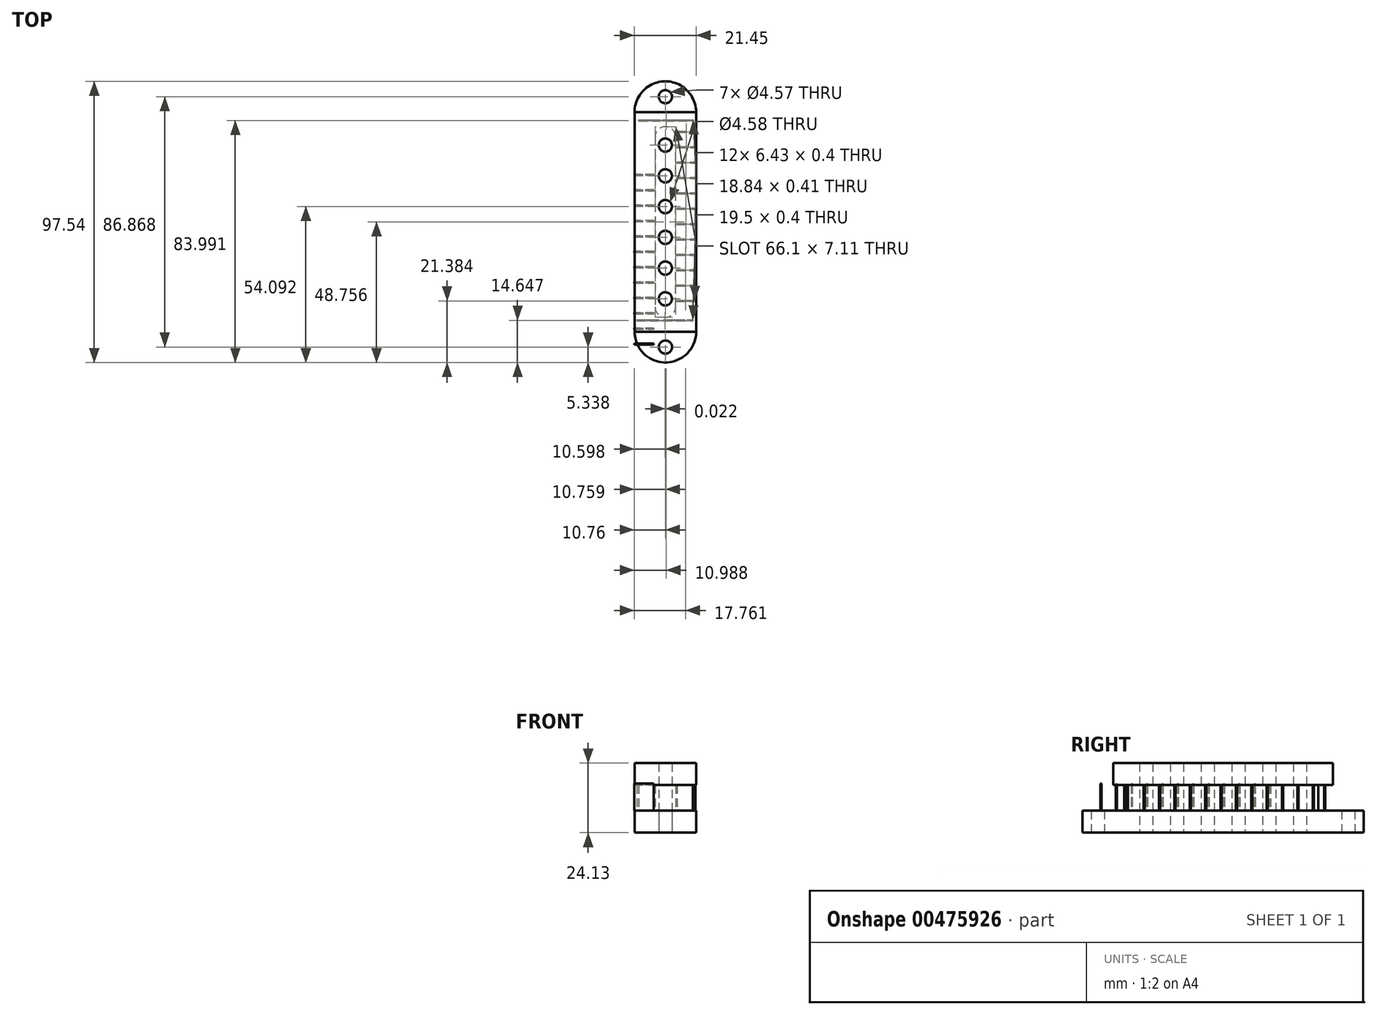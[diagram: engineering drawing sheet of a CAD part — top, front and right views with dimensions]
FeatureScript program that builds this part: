
annotation { "Feature Type Name" : "Feature", "Feature Type Description" : "" }
export const myFeature = defineFeature(function(context is Context, id is Id, definition is map)
    precondition{}
    {
        {
            var Q0;
            Q0=qCreatedBy(makeId("Top.planeOp"),FACE);
            var sketch = newSketch(context, id + "F0", { "sketchPlane" : qUnion([Q0])});
            skPoint(sketch, "E0.end.orphan", {"position": v(0, 0) * mm});
            skCircle(sketch, "E1", {"center": v(0, 12.62) * mm, "radius": 2.29 * mm});
            skCircle(sketch, "E2", {"center": v(0, 1.95) * mm, "radius": 2.29 * mm});
            skCircle(sketch, "E3", {"center": v(0, -8.72) * mm, "radius": 2.29 * mm});
            skCircle(sketch, "E4", {"center": v(0, -19.39) * mm, "radius": 2.29 * mm});
            skCircle(sketch, "E5", {"center": v(0, -30.06) * mm, "radius": 2.29 * mm});
            skCircle(sketch, "E6", {"center": v(0, -40.73) * mm, "radius": 2.29 * mm});
            skLineSegment(sketch, "E7", {"start": v(0, 24.06) * mm, "end": v(0, 14.92) * mm});
            skLineSegment(sketch, "E8", {"start": v(0, -52.14) * mm, "end": v(0, -43) * mm});
            skLineSegment(sketch, "E9", {"start": v(10.66, 24.07) * mm, "end": v(10.69, -52.13) * mm});
            skLineSegment(sketch, "E10", {"start": v(-10.69, 24.06) * mm, "end": v(-10.65, -52.14) * mm});
            skLineSegment(sketch, "E11", {"start": v(-10.69, 24.06) * mm, "end": v(10.66, 24.07) * mm});
            skLineSegment(sketch, "E12", {"start": v(-10.65, -52.14) * mm, "end": v(10.69, -52.13) * mm});
            skArc(sketch, "E13", {"start": v(-10.65, -52.14) * mm, "mid": v(0.03, -62.8) * mm, "end": v(10.69, -52.13) * mm});
            skArc(sketch, "E14", {"start": v(10.66, 24.07) * mm, "mid": v(-0.02, 34.73) * mm, "end": v(-10.69, 24.06) * mm});
            skCircle(sketch, "E15", {"center": v(0, 29.4) * mm, "radius": 2.29 * mm});
            skCircle(sketch, "E16", {"center": v(0.02, -57.47) * mm, "radius": 2.29 * mm});
            skSolve(sketch);
        }
        {
            var Q0;
            Q0 = qSketchRegion(id + "F0", true);
            extrude(context, id + "F1", {"entities" : qUnion([Q0]), "depth" : 7.62 * mm, "offsetDistance" : 25.4 * mm});
        }
        {
            var Q0;
            Q0=qCreatedBy(makeId("Top.planeOp"),FACE);
            var sketch = newSketch(context, id + "F2", { "sketchPlane" : qUnion([Q0])});
            skLineSegment(sketch, "E17", {"start": v(0, 0) * mm, "end": v(3.56, 0) * mm});
            skLineSegment(sketch, "E18", {"start": v(3.56, 0) * mm, "end": v(3.56, -43.55) * mm});
            skLineSegment(sketch, "E19", {"start": v(3.56, -43.55) * mm, "end": v(0, -43.55) * mm});
            skLineSegment(sketch, "E20", {"start": v(0, -43.55) * mm, "end": v(-3.56, -43.55) * mm});
            skPoint(sketch, "E20.endSnap0", {"position": v(1.78, -43.55) * mm});
            skLineSegment(sketch, "E21", {"start": v(-3.56, -43.55) * mm, "end": v(-3.56, 15.44) * mm});
            skLineSegment(sketch, "E22", {"start": v(-3.56, 15.44) * mm, "end": v(0, 15.44) * mm});
            skLineSegment(sketch, "E23", {"start": v(0, 15.44) * mm, "end": v(3.56, 15.44) * mm});
            skLineSegment(sketch, "E24", {"start": v(3.56, 15.44) * mm, "end": v(3.56, 0) * mm});
            skArc(sketch, "E25", {"start": v(-3.56, -43.55) * mm, "mid": v(0, -47.1) * mm, "end": v(3.56, -43.55) * mm});
            skArc(sketch, "E26", {"start": v(3.56, 15.44) * mm, "mid": v(0, 19) * mm, "end": v(-3.56, 15.44) * mm});
            skSolve(sketch);
        }
        {
            var Q0;
            Q0 = qSketchRegion(id + "F2", true);
            extrude(context, id + "F3", {"entities" : qUnion([Q0]), "operationType" : NewBodyOperationType.ADD, "depth" : 16.5 * mm, "offsetDistance" : 25.4 * mm});
        }
        {
            var Q0;
            Q0=makeQuery(id+"F3.opExtrude","CAP_FACE",FACE,{"disambiguationData":[OSD([sQuery(id+"F2.wireOp",EDGE,"E18"),sQuery(id+"F2.wireOp",EDGE,"E21"),sQuery(id+"F2.wireOp",EDGE,"E24"),sQuery(id+"F2.wireOp",EDGE,"E25"),sQuery(id+"F2.wireOp",EDGE,"E26")])],"isStart":false});
            var sketch = newSketch(context, id + "F4", { "sketchPlane" : qUnion([Q0])});
            skLineSegment(sketch, "E27", {"start": v(10.67, 0) * mm, "end": v(10.67, -52.15) * mm});
            skLineSegment(sketch, "E28", {"start": v(10.67, -52.15) * mm, "end": v(-10.67, -52.15) * mm});
            skLineSegment(sketch, "E29", {"start": v(-10.67, -52.15) * mm, "end": v(-10.67, 0) * mm});
            skLineSegment(sketch, "E30", {"start": v(-10.67, 0) * mm, "end": v(-10.67, 24.05) * mm});
            skLineSegment(sketch, "E31", {"start": v(-10.67, 24.05) * mm, "end": v(10.67, 24.05) * mm});
            skLineSegment(sketch, "E32", {"start": v(10.67, 24.05) * mm, "end": v(10.67, 0) * mm});
            skSolve(sketch);
        }
        {
            var Q0;
            Q0 = qSketchRegion(id + "F4", true);
            extrude(context, id + "F5", {"entities" : qUnion([Q0]), "operationType" : NewBodyOperationType.ADD, "depth" : 7.62 * mm, "offsetDistance" : 25.4 * mm});
        }
        {
            var Q0;
            Q0=makeQuery(id+"F0.imprint","IMPRINT",FACE,{"disambiguationData":[TD([[makeQuery(id+"F0.imprint","IMPRINT",EDGE,{"derivedFrom":sQuery(id+"F0.wireOp",EDGE,"E4")}),1.0]])]});
            var Q1;
            Q1=makeQuery(id+"F0.imprint","IMPRINT",FACE,{"disambiguationData":[TD([[makeQuery(id+"F0.imprint","IMPRINT",EDGE,{"derivedFrom":sQuery(id+"F0.wireOp",EDGE,"E6")}),1.0]])]});
            var Q2;
            Q2=makeQuery(id+"F0.imprint","IMPRINT",FACE,{"disambiguationData":[TD([[makeQuery(id+"F0.imprint","IMPRINT",EDGE,{"derivedFrom":sQuery(id+"F0.wireOp",EDGE,"E5")}),1.0]])]});
            var Q3;
            Q3=makeQuery(id+"F0.imprint","IMPRINT",FACE,{"disambiguationData":[TD([[makeQuery(id+"F0.imprint","IMPRINT",EDGE,{"derivedFrom":sQuery(id+"F0.wireOp",EDGE,"E3")}),1.0]])]});
            var Q4;
            Q4=makeQuery(id+"F0.imprint","IMPRINT",FACE,{"disambiguationData":[TD([[makeQuery(id+"F0.imprint","IMPRINT",EDGE,{"derivedFrom":sQuery(id+"F0.wireOp",EDGE,"E2")}),1.0]])]});
            var Q5;
            Q5=makeQuery(id+"F0.imprint","IMPRINT",FACE,{"disambiguationData":[TD([[makeQuery(id+"F0.imprint","IMPRINT",EDGE,{"derivedFrom":sQuery(id+"F0.wireOp",EDGE,"E1")}),1.0]])]});
            extrude(context, id + "F6", {"entities" : qUnion([Q0, Q1, Q2, Q3, Q4, Q5]), "operationType" : NewBodyOperationType.REMOVE, "endBound" : BoundingType.THROUGH_ALL, "depth" : 25.4 * mm, "offsetDistance" : 25.4 * mm});
        }
        {
            var Q0;
            Q0=makeQuery(id+"F1.opExtrude","CAP_FACE",FACE,{"disambiguationData":[OSD([sQuery(id+"F0.wireOp",EDGE,"E1"),sQuery(id+"F0.wireOp",EDGE,"E2"),sQuery(id+"F0.wireOp",EDGE,"E3"),sQuery(id+"F0.wireOp",EDGE,"E4"),sQuery(id+"F0.wireOp",EDGE,"E5"),sQuery(id+"F0.wireOp",EDGE,"E6"),sQuery(id+"F0.wireOp",EDGE,"E9"),sQuery(id+"F0.wireOp",EDGE,"E10"),sQuery(id+"F0.wireOp",EDGE,"E13"),sQuery(id+"F0.wireOp",EDGE,"E14"),sQuery(id+"F0.wireOp",EDGE,"E15"),sQuery(id+"F0.wireOp",EDGE,"E16")])],"isStart":false});
            var sketch = newSketch(context, id + "F7", { "sketchPlane" : qUnion([Q0])});
            skLineSegment(sketch, "E33.bottom", {"start": v(3.79, -41.63) * mm, "end": v(10.21, -41.63) * mm});
            skLineSegment(sketch, "E33.top", {"start": v(3.79, -41.23) * mm, "end": v(10.21, -41.23) * mm});
            skLineSegment(sketch, "E33.left", {"start": v(3.79, -41.63) * mm, "end": v(3.79, -41.23) * mm});
            skLineSegment(sketch, "E33.right", {"start": v(10.21, -41.63) * mm, "end": v(10.21, -41.23) * mm});
            skLineSegment(sketch, "E34.bottom", {"start": v(-9.91, -47.96) * mm, "end": v(9.59, -47.96) * mm});
            skLineSegment(sketch, "E34.top", {"start": v(-9.91, -48.36) * mm, "end": v(9.59, -48.36) * mm});
            skLineSegment(sketch, "E34.left", {"start": v(-9.91, -47.96) * mm, "end": v(-9.91, -48.36) * mm});
            skLineSegment(sketch, "E34.right", {"start": v(9.59, -47.96) * mm, "end": v(9.59, -48.36) * mm});
            skLineSegment(sketch, "E35.0.1.0", {"start": v(3.8, -36.3) * mm, "end": v(3.8, -35.9) * mm});
            skLineSegment(sketch, "E35.0.1.1", {"start": v(3.8, -35.9) * mm, "end": v(10.24, -35.9) * mm});
            skLineSegment(sketch, "E35.0.1.2", {"start": v(10.24, -36.3) * mm, "end": v(10.24, -35.9) * mm});
            skLineSegment(sketch, "E35.0.1.3", {"start": v(3.8, -36.3) * mm, "end": v(10.24, -36.3) * mm});
            skLineSegment(sketch, "E35.0.2.0", {"start": v(3.83, -30.96) * mm, "end": v(3.83, -30.56) * mm});
            skLineSegment(sketch, "E35.0.2.1", {"start": v(3.83, -30.56) * mm, "end": v(10.26, -30.56) * mm});
            skLineSegment(sketch, "E35.0.2.2", {"start": v(10.26, -30.96) * mm, "end": v(10.26, -30.56) * mm});
            skLineSegment(sketch, "E35.0.2.3", {"start": v(3.83, -30.96) * mm, "end": v(10.26, -30.96) * mm});
            skLineSegment(sketch, "E35.0.3.0", {"start": v(3.85, -25.62) * mm, "end": v(3.85, -25.22) * mm});
            skLineSegment(sketch, "E35.0.3.1", {"start": v(3.85, -25.22) * mm, "end": v(10.28, -25.22) * mm});
            skLineSegment(sketch, "E35.0.3.2", {"start": v(10.28, -25.62) * mm, "end": v(10.28, -25.22) * mm});
            skLineSegment(sketch, "E35.0.3.3", {"start": v(3.85, -25.62) * mm, "end": v(10.28, -25.62) * mm});
            skLineSegment(sketch, "E35.0.4.0", {"start": v(3.87, -20.3) * mm, "end": v(3.87, -19.9) * mm});
            skLineSegment(sketch, "E35.0.4.1", {"start": v(3.87, -19.9) * mm, "end": v(10.3, -19.9) * mm});
            skLineSegment(sketch, "E35.0.4.2", {"start": v(10.3, -20.3) * mm, "end": v(10.3, -19.9) * mm});
            skLineSegment(sketch, "E35.0.4.3", {"start": v(3.87, -20.3) * mm, "end": v(10.3, -20.3) * mm});
            skLineSegment(sketch, "E35.0.5.0", {"start": v(3.9, -14.96) * mm, "end": v(3.9, -14.56) * mm});
            skLineSegment(sketch, "E35.0.5.1", {"start": v(3.9, -14.56) * mm, "end": v(10.32, -14.56) * mm});
            skLineSegment(sketch, "E35.0.5.2", {"start": v(10.32, -14.96) * mm, "end": v(10.32, -14.56) * mm});
            skLineSegment(sketch, "E35.0.5.3", {"start": v(3.9, -14.96) * mm, "end": v(10.32, -14.96) * mm});
            skLineSegment(sketch, "E35.0.6.0", {"start": v(3.92, -9.62) * mm, "end": v(3.92, -9.22) * mm});
            skLineSegment(sketch, "E35.0.6.1", {"start": v(3.92, -9.22) * mm, "end": v(10.34, -9.22) * mm});
            skLineSegment(sketch, "E35.0.6.2", {"start": v(10.34, -9.62) * mm, "end": v(10.34, -9.22) * mm});
            skLineSegment(sketch, "E35.0.6.3", {"start": v(3.92, -9.62) * mm, "end": v(10.34, -9.62) * mm});
            skLineSegment(sketch, "E35.0.7.0", {"start": v(3.94, -4.29) * mm, "end": v(3.94, -3.89) * mm});
            skLineSegment(sketch, "E35.0.7.1", {"start": v(3.94, -3.89) * mm, "end": v(10.37, -3.89) * mm});
            skLineSegment(sketch, "E35.0.7.2", {"start": v(10.37, -4.29) * mm, "end": v(10.37, -3.89) * mm});
            skLineSegment(sketch, "E35.0.7.3", {"start": v(3.94, -4.29) * mm, "end": v(10.37, -4.29) * mm});
            skLineSegment(sketch, "E35.0.8.0", {"start": v(3.96, 1.05) * mm, "end": v(3.96, 1.45) * mm});
            skLineSegment(sketch, "E35.0.8.1", {"start": v(3.96, 1.45) * mm, "end": v(10.39, 1.45) * mm});
            skLineSegment(sketch, "E35.0.8.2", {"start": v(10.39, 1.05) * mm, "end": v(10.39, 1.45) * mm});
            skLineSegment(sketch, "E35.0.8.3", {"start": v(3.96, 1.05) * mm, "end": v(10.39, 1.05) * mm});
            skLineSegment(sketch, "E35.0.9.0", {"start": v(3.98, 6.38) * mm, "end": v(3.98, 6.78) * mm});
            skLineSegment(sketch, "E35.0.9.1", {"start": v(3.98, 6.78) * mm, "end": v(10.4, 6.78) * mm});
            skLineSegment(sketch, "E35.0.9.2", {"start": v(10.4, 6.38) * mm, "end": v(10.4, 6.78) * mm});
            skLineSegment(sketch, "E35.0.9.3", {"start": v(3.98, 6.38) * mm, "end": v(10.4, 6.38) * mm});
            skLineSegment(sketch, "E35.0.10.0", {"start": v(4, 11.71) * mm, "end": v(4, 12.11) * mm});
            skLineSegment(sketch, "E35.0.10.1", {"start": v(4, 12.11) * mm, "end": v(10.43, 12.11) * mm});
            skLineSegment(sketch, "E35.0.10.2", {"start": v(10.43, 11.71) * mm, "end": v(10.43, 12.11) * mm});
            skLineSegment(sketch, "E35.0.10.3", {"start": v(4, 11.71) * mm, "end": v(10.43, 11.71) * mm});
            skLineSegment(sketch, "E35.0.11.0", {"start": v(4.03, 17.05) * mm, "end": v(4.03, 17.45) * mm});
            skLineSegment(sketch, "E35.0.11.1", {"start": v(4.03, 17.45) * mm, "end": v(10.45, 17.45) * mm});
            skLineSegment(sketch, "E35.0.11.2", {"start": v(10.45, 17.05) * mm, "end": v(10.45, 17.45) * mm});
            skLineSegment(sketch, "E35.0.11.3", {"start": v(4.03, 17.05) * mm, "end": v(10.45, 17.05) * mm});
            skLineSegment(sketch, "E35.direction1", {"start": v(3.79, -41.63) * mm, "end": v(3.85, -0.22) * mm, "construction": true});
            skLineSegment(sketch, "E35.direction2", {"start": v(3.79, -41.63) * mm, "end": v(3.8, -36.3) * mm, "construction": true});
            skLineSegment(sketch, "E36.bottom", {"start": v(-9.2, 20.98) * mm, "end": v(9.65, 20.98) * mm});
            skLineSegment(sketch, "E36.top", {"start": v(-9.2, 21.38) * mm, "end": v(9.65, 21.38) * mm});
            skLineSegment(sketch, "E36.left", {"start": v(-9.2, 20.98) * mm, "end": v(-9.2, 21.38) * mm});
            skLineSegment(sketch, "E36.right", {"start": v(9.65, 20.98) * mm, "end": v(9.65, 21.38) * mm});
            skLineSegment(sketch, "E37.bottom", {"start": v(-10.68, 2.46) * mm, "end": v(-3.93, 2.46) * mm});
            skLineSegment(sketch, "E37.top", {"start": v(-10.68, 2.05) * mm, "end": v(-3.93, 2.05) * mm});
            skLineSegment(sketch, "E37.left", {"start": v(-10.68, 2.46) * mm, "end": v(-10.68, 2.05) * mm});
            skLineSegment(sketch, "E37.right", {"start": v(-3.93, 2.46) * mm, "end": v(-3.93, 2.05) * mm});
            skLineSegment(sketch, "E38.0.1.0", {"start": v(-10.68, -2.88) * mm, "end": v(-3.94, -2.88) * mm});
            skLineSegment(sketch, "E38.0.1.1", {"start": v(-10.68, -3.29) * mm, "end": v(-3.94, -3.29) * mm});
            skLineSegment(sketch, "E38.0.1.2", {"start": v(-10.68, -2.88) * mm, "end": v(-10.68, -3.29) * mm});
            skLineSegment(sketch, "E38.0.1.3", {"start": v(-3.94, -2.88) * mm, "end": v(-3.94, -3.29) * mm});
            skLineSegment(sketch, "E38.0.2.0", {"start": v(-10.7, -8.21) * mm, "end": v(-3.95, -8.21) * mm});
            skLineSegment(sketch, "E38.0.2.1", {"start": v(-10.7, -8.62) * mm, "end": v(-3.95, -8.62) * mm});
            skLineSegment(sketch, "E38.0.2.2", {"start": v(-10.7, -8.21) * mm, "end": v(-10.7, -8.62) * mm});
            skLineSegment(sketch, "E38.0.2.3", {"start": v(-3.95, -8.21) * mm, "end": v(-3.95, -8.62) * mm});
            skLineSegment(sketch, "E38.0.3.0", {"start": v(-10.7, -13.55) * mm, "end": v(-3.95, -13.55) * mm});
            skLineSegment(sketch, "E38.0.3.1", {"start": v(-10.7, -13.95) * mm, "end": v(-3.95, -13.95) * mm});
            skLineSegment(sketch, "E38.0.3.2", {"start": v(-10.7, -13.55) * mm, "end": v(-10.7, -13.95) * mm});
            skLineSegment(sketch, "E38.0.3.3", {"start": v(-3.95, -13.55) * mm, "end": v(-3.95, -13.95) * mm});
            skLineSegment(sketch, "E38.0.4.0", {"start": v(-10.7, -18.88) * mm, "end": v(-3.96, -18.88) * mm});
            skLineSegment(sketch, "E38.0.4.1", {"start": v(-10.7, -19.29) * mm, "end": v(-3.96, -19.29) * mm});
            skLineSegment(sketch, "E38.0.4.2", {"start": v(-10.7, -18.88) * mm, "end": v(-10.7, -19.29) * mm});
            skLineSegment(sketch, "E38.0.4.3", {"start": v(-3.96, -18.88) * mm, "end": v(-3.96, -19.29) * mm});
            skLineSegment(sketch, "E38.0.5.0", {"start": v(-10.71, -24.21) * mm, "end": v(-3.97, -24.21) * mm});
            skLineSegment(sketch, "E38.0.5.1", {"start": v(-10.71, -24.62) * mm, "end": v(-3.97, -24.62) * mm});
            skLineSegment(sketch, "E38.0.5.2", {"start": v(-10.71, -24.21) * mm, "end": v(-10.71, -24.62) * mm});
            skLineSegment(sketch, "E38.0.5.3", {"start": v(-3.97, -24.21) * mm, "end": v(-3.97, -24.62) * mm});
            skLineSegment(sketch, "E38.0.6.0", {"start": v(-10.72, -29.55) * mm, "end": v(-3.98, -29.55) * mm});
            skLineSegment(sketch, "E38.0.6.1", {"start": v(-10.72, -29.96) * mm, "end": v(-3.98, -29.96) * mm});
            skLineSegment(sketch, "E38.0.6.2", {"start": v(-10.72, -29.55) * mm, "end": v(-10.72, -29.96) * mm});
            skLineSegment(sketch, "E38.0.6.3", {"start": v(-3.98, -29.55) * mm, "end": v(-3.98, -29.96) * mm});
            skLineSegment(sketch, "E38.0.7.0", {"start": v(-10.73, -34.88) * mm, "end": v(-3.98, -34.88) * mm});
            skLineSegment(sketch, "E38.0.7.1", {"start": v(-10.73, -35.29) * mm, "end": v(-3.98, -35.29) * mm});
            skLineSegment(sketch, "E38.0.7.2", {"start": v(-10.73, -34.88) * mm, "end": v(-10.73, -35.29) * mm});
            skLineSegment(sketch, "E38.0.7.3", {"start": v(-3.98, -34.88) * mm, "end": v(-3.98, -35.29) * mm});
            skLineSegment(sketch, "E38.0.8.0", {"start": v(-10.74, -40.22) * mm, "end": v(-4, -40.22) * mm});
            skLineSegment(sketch, "E38.0.8.1", {"start": v(-10.74, -40.62) * mm, "end": v(-4, -40.62) * mm});
            skLineSegment(sketch, "E38.0.8.2", {"start": v(-10.74, -40.22) * mm, "end": v(-10.74, -40.62) * mm});
            skLineSegment(sketch, "E38.0.8.3", {"start": v(-4, -40.22) * mm, "end": v(-4, -40.62) * mm});
            skLineSegment(sketch, "E38.0.9.0", {"start": v(-10.74, -45.55) * mm, "end": v(-4, -45.55) * mm});
            skLineSegment(sketch, "E38.0.9.1", {"start": v(-10.74, -45.96) * mm, "end": v(-4, -45.96) * mm});
            skLineSegment(sketch, "E38.0.9.2", {"start": v(-10.74, -45.55) * mm, "end": v(-10.74, -45.96) * mm});
            skLineSegment(sketch, "E38.0.9.3", {"start": v(-4, -45.55) * mm, "end": v(-4, -45.96) * mm});
            skLineSegment(sketch, "E38.0.10.0", {"start": v(-10.75, -50.88) * mm, "end": v(-4, -50.88) * mm});
            skLineSegment(sketch, "E38.0.10.1", {"start": v(-10.75, -51.3) * mm, "end": v(-4, -51.3) * mm});
            skLineSegment(sketch, "E38.0.10.2", {"start": v(-10.75, -50.88) * mm, "end": v(-10.75, -51.3) * mm});
            skLineSegment(sketch, "E38.0.10.3", {"start": v(-4, -50.88) * mm, "end": v(-4, -51.3) * mm});
            skLineSegment(sketch, "E38.0.11.0", {"start": v(-10.76, -56.22) * mm, "end": v(-4.01, -56.22) * mm});
            skLineSegment(sketch, "E38.0.11.1", {"start": v(-10.76, -56.63) * mm, "end": v(-4.01, -56.63) * mm});
            skLineSegment(sketch, "E38.0.11.2", {"start": v(-10.76, -56.22) * mm, "end": v(-10.76, -56.63) * mm});
            skLineSegment(sketch, "E38.0.11.3", {"start": v(-4.01, -56.22) * mm, "end": v(-4.01, -56.63) * mm});
            skLineSegment(sketch, "E38.direction1", {"start": v(-10.68, 2.46) * mm, "end": v(14.72, 2.46) * mm, "construction": true});
            skLineSegment(sketch, "E38.direction2", {"start": v(-10.68, 2.46) * mm, "end": v(-10.68, -2.88) * mm, "construction": true});
            skSolve(sketch);
        }
        {
            var Q0;
            Q0 = qSketchRegion(id + "F7", true);
            extrude(context, id + "F8", {"entities" : qUnion([Q0]), "operationType" : NewBodyOperationType.ADD, "depth" : 9.4 * mm, "offsetDistance" : 25.4 * mm});
        }
    });
